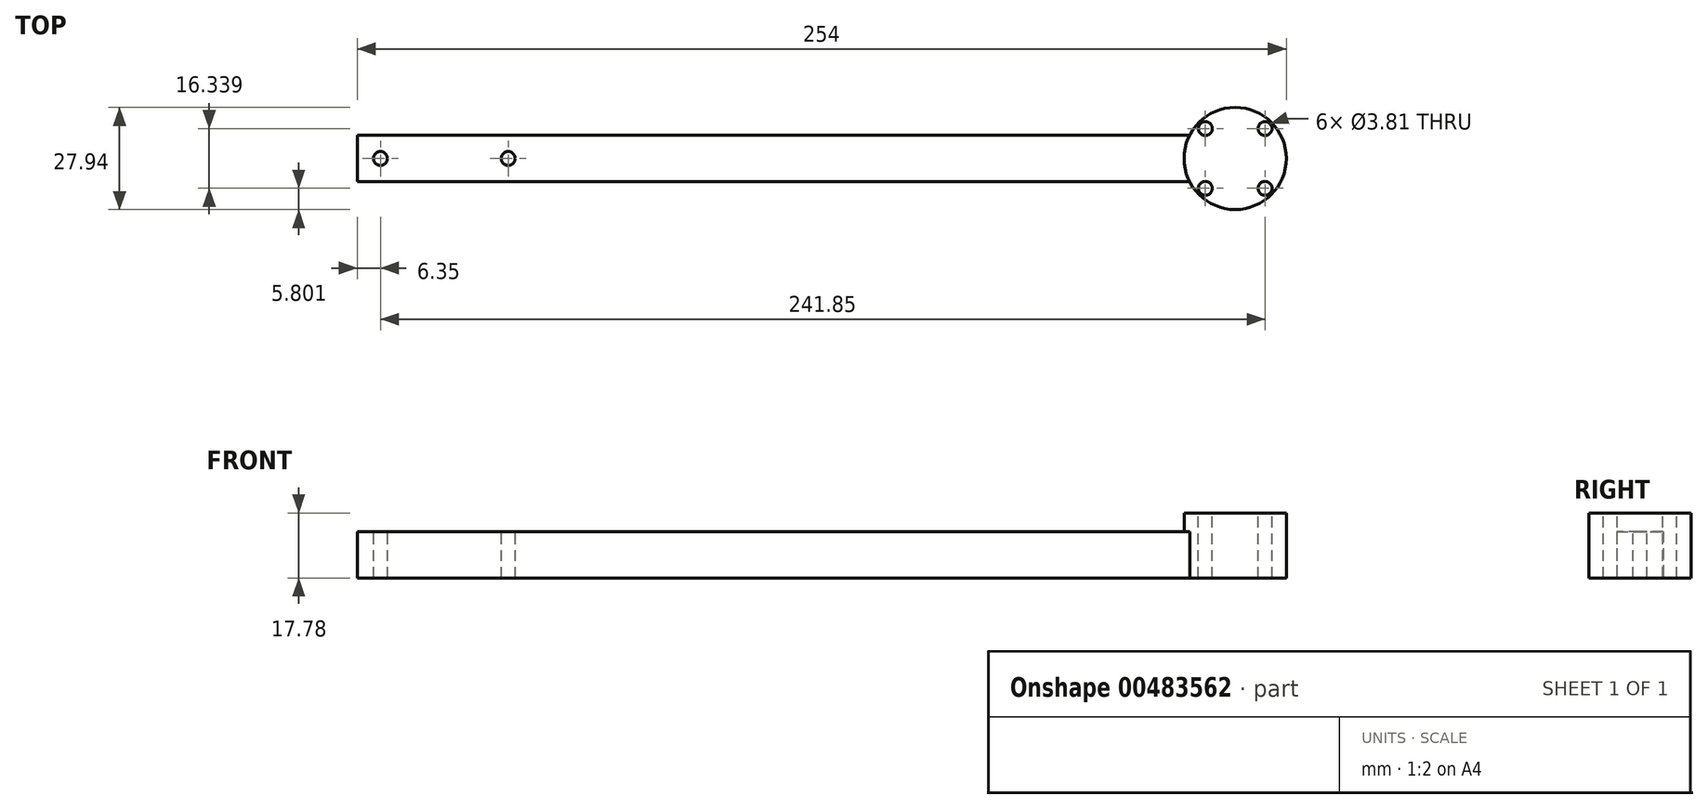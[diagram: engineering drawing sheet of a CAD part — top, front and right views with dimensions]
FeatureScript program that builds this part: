
annotation { "Feature Type Name" : "Feature", "Feature Type Description" : "" }
export const myFeature = defineFeature(function(context is Context, id is Id, definition is map)
    precondition{}
    {
        {
            var Q0;
            Q0=qCreatedBy(makeId("Front.planeOp"),FACE);
            var sketch = newSketch(context, id + "F0", { "sketchPlane" : qUnion([Q0])});
            skLineSegment(sketch, "E0.bottom", {"start": v(-240.03, 12.7) * mm, "end": v(0, 12.7) * mm});
            skLineSegment(sketch, "E0.top", {"start": v(-240.03, 0) * mm, "end": v(0, 0) * mm});
            skLineSegment(sketch, "E0.left", {"start": v(-240.03, 12.7) * mm, "end": v(-240.03, 0) * mm});
            skLineSegment(sketch, "E0.right", {"start": v(0, 12.7) * mm, "end": v(0, 0) * mm});
            skSolve(sketch);
        }
        {
            var Q0;
            Q0=makeQuery(id+"F0.imprint","IMPRINT",FACE,{"disambiguationData":[TD([[makeQuery(id+"F0.imprint","IMPRINT",EDGE,{"derivedFrom":sQuery(id+"F0.wireOp",EDGE,"E0.bottom")}),-1.0]])]});
            extrude(context, id + "F1", {"entities" : qUnion([Q0]), "depth" : 6.35 * mm, "hasSecondDirection" : true, "secondDirectionOppositeDirection" : true, "secondDirectionDepth" : 6.35 * mm});
        }
        {
            var Q0;
            Q0=makeQuery(id+"F1.opExtrude","SWEPT_FACE",FACE,{"disambiguationData":[OSD([sQuery(id+"F0.wireOp",EDGE,"E0.top")])]});
            var sketch = newSketch(context, id + "F2", { "sketchPlane" : qUnion([Q0])});
            skCircle(sketch, "E1", {"center": v(0, 0) * mm, "radius": 13.97 * mm});
            skSolve(sketch);
        }
        {
            var Q0;
            Q0 = qSketchRegion(id + "F2", true);
            extrude(context, id + "F3", {"entities" : qUnion([Q0]), "operationType" : NewBodyOperationType.ADD, "oppositeDirection" : true, "depth" : 17.78 * mm});
        }
        {
            var Q0;
            Q0=makeQuery(id+"F1.opExtrude","SWEPT_FACE",FACE,{"disambiguationData":[OSD([sQuery(id+"F0.wireOp",EDGE,"E0.bottom")])]});
            var sketch = newSketch(context, id + "F4", { "sketchPlane" : qUnion([Q0])});
            skPoint(sketch, "E2", {"position": v(-233.68, 0) * mm});
            skPoint(sketch, "E3", {"position": v(-198.75, 0) * mm});
            skSolve(sketch);
        }
        {
            var Q0;
            Q0=sQuery(id+"F4.wireOp",VERTEX,"E2");
            var Q1;
            Q1=sQuery(id+"F4.wireOp",VERTEX,"E3");
            var Q2;
            Q2=makeQuery(id+"F1.opExtrude","SWEPT_BODY",BODY,{"disambiguationData":[OSD([sQuery(id+"F0.wireOp",EDGE,"E0.bottom"),sQuery(id+"F0.wireOp",EDGE,"E0.top"),sQuery(id+"F0.wireOp",EDGE,"E0.left"),sQuery(id+"F0.wireOp",EDGE,"E0.right")])]});
            hole(context, id + "F5", {"style" : HoleStyle.SIMPLE, "endStyle" : HoleEndStyle.THROUGH, "holeDiameter" : 3.8 * mm, "isTappedThrough" : true, "tappedDepth" : 12.7 * mm, "tapClearance" : 3, "startFromSketch" : true, "locations" : qUnion([Q0, Q1]), "scope" : qUnion([Q2])});
        }
        {
            var Q0;
            Q0=makeQuery(id+"F3.opExtrude","CAP_FACE",FACE,{"disambiguationData":[OSD([sQuery(id+"F2.wireOp",EDGE,"E1")])],"isStart":false});
            var sketch = newSketch(context, id + "F6", { "sketchPlane" : qUnion([Q0])});
            skPoint(sketch, "E4", {"position": v(-8.17, 8.17) * mm});
            skPoint(sketch, "E5", {"position": v(8.17, -8.17) * mm});
            skPoint(sketch, "E6", {"position": v(-8.17, -8.17) * mm});
            skPoint(sketch, "E7", {"position": v(8.17, 8.17) * mm});
            skLineSegment(sketch, "E8", {"start": v(-8.17, -8.17) * mm, "end": v(8.17, 8.17) * mm, "construction": true});
            skLineSegment(sketch, "E9", {"start": v(-8.17, 8.17) * mm, "end": v(8.17, -8.17) * mm, "construction": true});
            skCircle(sketch, "E10", {"center": v(0, 0) * mm, "radius": 11.55 * mm, "construction": true});
            skSolve(sketch);
        }
        {
            var Q0;
            Q0=sQuery(id+"F6.wireOp",VERTEX,"E4");
            var Q1;
            Q1=sQuery(id+"F6.wireOp",VERTEX,"E7");
            var Q2;
            Q2=sQuery(id+"F6.wireOp",VERTEX,"E5");
            var Q3;
            Q3=sQuery(id+"F6.wireOp",VERTEX,"E6");
            var Q4;
            Q4=makeQuery(id+"F1.opExtrude","SWEPT_BODY",BODY,{"disambiguationData":[OSD([sQuery(id+"F0.wireOp",EDGE,"E0.bottom"),sQuery(id+"F0.wireOp",EDGE,"E0.top"),sQuery(id+"F0.wireOp",EDGE,"E0.left"),sQuery(id+"F0.wireOp",EDGE,"E0.right")])]});
            hole(context, id + "F7", {"style" : HoleStyle.SIMPLE, "endStyle" : HoleEndStyle.THROUGH, "holeDiameter" : 3.8 * mm, "isTappedThrough" : true, "tappedDepth" : 12.7 * mm, "tapClearance" : 3, "startFromSketch" : true, "locations" : qUnion([Q0, Q1, Q2, Q3]), "scope" : qUnion([Q4])});
        }
    });
